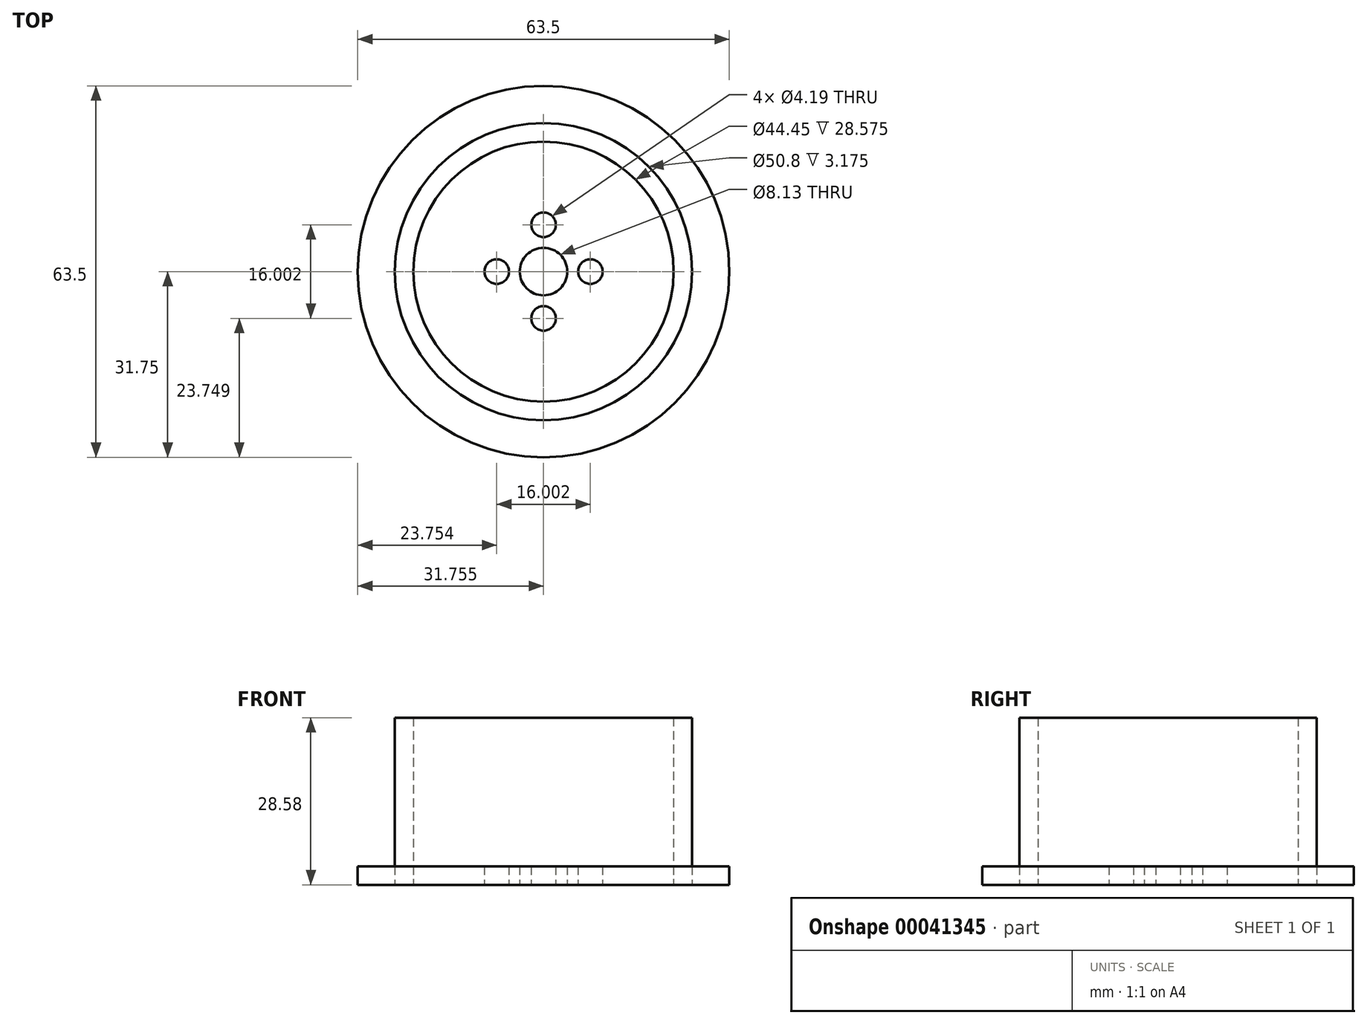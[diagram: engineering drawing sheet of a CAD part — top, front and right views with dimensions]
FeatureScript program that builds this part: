
annotation { "Feature Type Name" : "Feature", "Feature Type Description" : "" }
export const myFeature = defineFeature(function(context is Context, id is Id, definition is map)
    precondition{}
    {
        {
            var Q0;
            Q0=qCreatedBy(makeId("Top.planeOp"),FACE);
            var sketch = newSketch(context, id + "F0", { "sketchPlane" : qUnion([Q0])});
            skCircle(sketch, "E0", {"center": v(-126.67, 32.56) * mm, "radius": 31.75 * mm});
            skCircle(sketch, "E1.0", {"center": v(-126.67, 32.56) * mm, "radius": 25.4 * mm});
            skCircle(sketch, "E2", {"center": v(-126.67, 32.56) * mm, "radius": 4.06 * mm});
            skCircle(sketch, "E3", {"center": v(-126.67, 40.56) * mm, "radius": 2.1 * mm});
            skCircle(sketch, "E4", {"center": v(-118.66, 32.56) * mm, "radius": 2.1 * mm});
            skCircle(sketch, "E5", {"center": v(-126.67, 24.56) * mm, "radius": 2.1 * mm});
            skCircle(sketch, "E6", {"center": v(-134.67, 32.56) * mm, "radius": 2.1 * mm});
            skCircle(sketch, "E7", {"center": v(-126.67, 32.56) * mm, "radius": 22.23 * mm});
            skSolve(sketch);
        }
        {
            var Q0;
            Q0=makeQuery(id+"F0.imprint","IMPRINT",FACE,{"disambiguationData":[TD([[makeQuery(id+"F0.imprint","IMPRINT",EDGE,{"derivedFrom":sQuery(id+"F0.wireOp",EDGE,"E2")}),-1.0]])]});
            var Q1;
            Q1=makeQuery(id+"F0.imprint","IMPRINT",FACE,{"disambiguationData":[TD([[makeQuery(id+"F0.imprint","IMPRINT",EDGE,{"derivedFrom":sQuery(id+"F0.wireOp",EDGE,"E0")}),1.0]])]});
            extrude(context, id + "F1", {"entities" : qUnion([Q0, Q1]), "depth" : 3.17 * mm});
        }
        {
            var Q0;
            Q0=makeQuery(id+"F0.imprint","IMPRINT",FACE,{"disambiguationData":[TD([[makeQuery(id+"F0.imprint","IMPRINT",EDGE,{"derivedFrom":sQuery(id+"F0.wireOp",EDGE,"E1.0")}),1.0]])]});
            extrude(context, id + "F2", {"entities" : qUnion([Q0]), "depth" : 28.57 * mm});
        }
    });
